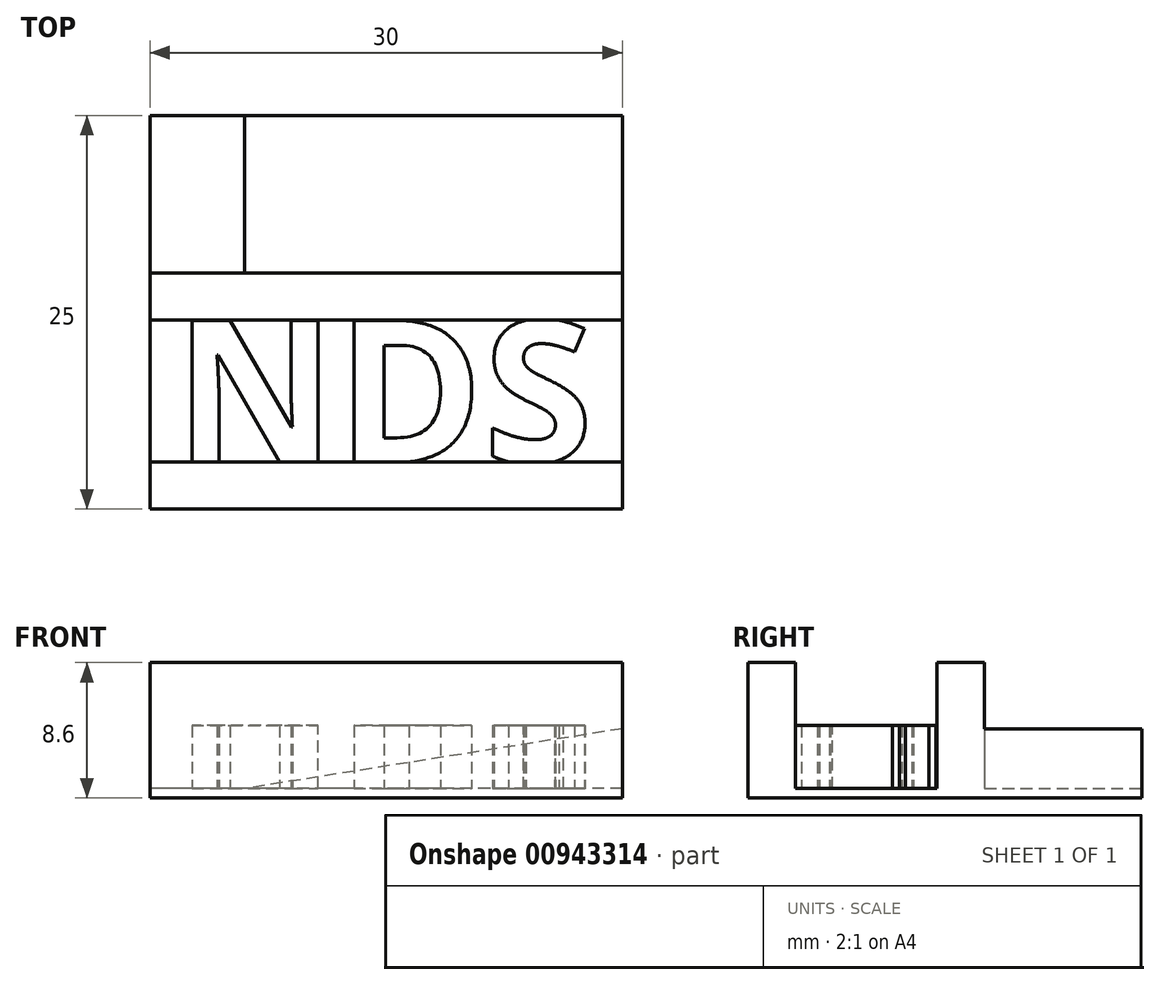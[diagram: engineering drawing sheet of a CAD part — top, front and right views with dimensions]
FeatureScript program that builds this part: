
annotation { "Feature Type Name" : "Feature", "Feature Type Description" : "" }
export const myFeature = defineFeature(function(context is Context, id is Id, definition is map)
    precondition{}
    {
        {
            var Q0;
            Q0=qCreatedBy(makeId("Top.planeOp"),FACE);
            var sketch = newSketch(context, id + "F0", { "sketchPlane" : qUnion([Q0])});
            skLineSegment(sketch, "E0.bottom", {"start": v(0, 0) * mm, "end": v(-30, 0) * mm});
            skLineSegment(sketch, "E0.top", {"start": v(0, 15) * mm, "end": v(-30, 15) * mm});
            skLineSegment(sketch, "E0.left", {"start": v(0, 0) * mm, "end": v(0, 15) * mm});
            skLineSegment(sketch, "E0.right", {"start": v(-30, 0) * mm, "end": v(-30, 15) * mm});
            skLineSegment(sketch, "E1.top", {"start": v(0, 25) * mm, "end": v(-30, 25) * mm});
            skLineSegment(sketch, "E1.left", {"start": v(0, 15) * mm, "end": v(0, 25) * mm});
            skLineSegment(sketch, "E1.right", {"start": v(-30, 15) * mm, "end": v(-30, 25) * mm});
            skSolve(sketch);
        }
        {
            var Q0;
            Q0=makeQuery(id+"F0.imprint","IMPRINT",FACE,{"disambiguationData":[TD([[makeQuery(id+"F0.imprint","IMPRINT",EDGE,{"derivedFrom":sQuery(id+"F0.wireOp",EDGE,"E0.top")}),-1.0]])]});
            var Q1;
            Q1=makeQuery(id+"F0.imprint","IMPRINT",FACE,{"disambiguationData":[TD([[makeQuery(id+"F0.imprint","IMPRINT",EDGE,{"derivedFrom":sQuery(id+"F0.wireOp",EDGE,"E0.bottom")}),-1.0]])]});
            extrude(context, id + "F1", {"entities" : qUnion([Q0, Q1]), "depth" : 0.6 * mm, "offsetDistance" : 25 * mm});
        }
        {
            var Q0;
            Q0=makeQuery(id+"F1.opExtrude","CAP_FACE",FACE,{"disambiguationData":[OSD([sQuery(id+"F0.wireOp",EDGE,"E0.bottom"),sQuery(id+"F0.wireOp",EDGE,"E0.left"),sQuery(id+"F0.wireOp",EDGE,"E0.right"),sQuery(id+"F0.wireOp",EDGE,"E1.top"),sQuery(id+"F0.wireOp",EDGE,"E1.left"),sQuery(id+"F0.wireOp",EDGE,"E1.right")])],"isStart":false});
            var sketch = newSketch(context, id + "F2", { "sketchPlane" : qUnion([Q0])});
            skLineSegment(sketch, "E2.bottom", {"start": v(0, 0) * mm, "end": v(-30, 0) * mm});
            skLineSegment(sketch, "E2.top", {"start": v(0, 15) * mm, "end": v(-30, 15) * mm});
            skLineSegment(sketch, "E2.left", {"start": v(0, 0) * mm, "end": v(0, 15) * mm});
            skLineSegment(sketch, "E2.right", {"start": v(-30, 0) * mm, "end": v(-30, 15) * mm});
            skLineSegment(sketch, "E3.top", {"start": v(0, 12) * mm, "end": v(-30, 12) * mm});
            skLineSegment(sketch, "E3.left", {"start": v(0, 15) * mm, "end": v(0, 12) * mm});
            skLineSegment(sketch, "E3.right", {"start": v(-30, 15) * mm, "end": v(-30, 12) * mm});
            skLineSegment(sketch, "E4.top", {"start": v(0, 3) * mm, "end": v(-30, 3) * mm});
            skLineSegment(sketch, "E4.left", {"start": v(0, 0) * mm, "end": v(0, 3) * mm});
            skLineSegment(sketch, "E4.right", {"start": v(-30, 0) * mm, "end": v(-30, 3) * mm});
            skSolve(sketch);
        }
        {
            var Q0;
            Q0=makeQuery(id+"F2.imprint","IMPRINT",FACE,{"disambiguationData":[TD([[makeQuery(id+"F2.imprint","IMPRINT",EDGE,{"derivedFrom":sQuery(id+"F2.wireOp",EDGE,"E2.top")}),1.0]])]});
            var Q1;
            Q1=makeQuery(id+"F2.imprint","IMPRINT",FACE,{"disambiguationData":[TD([[makeQuery(id+"F2.imprint","IMPRINT",EDGE,{"derivedFrom":sQuery(id+"F2.wireOp",EDGE,"E2.bottom")}),-1.0]])]});
            extrude(context, id + "F3", {"entities" : qUnion([Q0, Q1]), "operationType" : NewBodyOperationType.ADD, "depth" : 8 * mm, "offsetDistance" : 25 * mm});
        }
        {
            var Q0;
            Q0=makeQuery(id+"F3.opExtrude","SWEPT_FACE",FACE,{"disambiguationData":[OSD([sQuery(id+"F2.wireOp",EDGE,"E2.top")])]});
            var sketch = newSketch(context, id + "F4", { "sketchPlane" : qUnion([Q0])});
            skLineSegment(sketch, "E5.bottom", {"start": v(0, 8.6) * mm, "end": v(24, 8.6) * mm});
            skLineSegment(sketch, "E5.top", {"start": v(0, 0.6) * mm, "end": v(24, 0.6) * mm});
            skLineSegment(sketch, "E5.left", {"start": v(0, 8.6) * mm, "end": v(0, 0.6) * mm});
            skLineSegment(sketch, "E5.right", {"start": v(24, 8.6) * mm, "end": v(24, 0.6) * mm});
            skLineSegment(sketch, "E6", {"start": v(0, 0.6) * mm, "end": v(0, 4.4) * mm});
            skLineSegment(sketch, "E7", {"start": v(0, 4.4) * mm, "end": v(24, 0.6) * mm});
            skSolve(sketch);
        }
        {
            var Q0;
            Q0=makeQuery(id+"F4.imprint","IMPRINT",FACE,{"disambiguationData":[TD([[makeQuery(id+"F4.imprint","IMPRINT",EDGE,{"derivedFrom":sQuery(id+"F4.wireOp",EDGE,"E5.top")}),1.0]])]});
            extrude(context, id + "F5", {"entities" : qUnion([Q0]), "operationType" : NewBodyOperationType.ADD, "depth" : 10 * mm, "offsetDistance" : 25 * mm});
        }
        {
            var Q0;
            {var subQ0=sQuery(id+"F0.wireOp",EDGE,"E1.right");var subQ1=sQuery(id+"F0.wireOp",EDGE,"E0.right");var subQ2=sQuery(id+"F0.wireOp",EDGE,"E1.left");var subQ3=sQuery(id+"F0.wireOp",EDGE,"E0.left");Q0=makeQuery(id+"F3.boolean.opBoolean","SPLIT",FACE,{"disambiguationData":[TD([makeQuery(id+"F3.opExtrude","SWEPT_FACE",FACE,{"disambiguationData":[OSD([sQuery(id+"F2.wireOp",EDGE,"E3.top")])]})])],"derivedFrom":makeQuery(id+"F1.opExtrude","CAP_FACE",FACE,{"disambiguationData":[OSD([sQuery(id+"F0.wireOp",EDGE,"E0.bottom"),subQ3,subQ1,sQuery(id+"F0.wireOp",EDGE,"E1.top"),subQ2,subQ0])],"isStart":false})});}
            var sketch = newSketch(context, id + "F6", { "sketchPlane" : qUnion([Q0])});
            skText(sketch, "E8", { "text": "NDS", "fontName": "OpenSans-Bold.ttf"});
            skLineSegment(sketch, "E9", {"start": v(-28.46, 12.05) * mm, "end": v(-30, 12.05) * mm});
            skLineSegment(sketch, "E10", {"start": v(-1.54, 12.05) * mm, "end": v(0, 12.05) * mm});
            skLineSegment(sketch, "E11", {"start": v(-28.46, 12) * mm, "end": v(-28.46, 12.05) * mm});
            skLineSegment(sketch, "E12", {"start": v(-28.46, 3) * mm, "end": v(-28.46, 2.95) * mm});
            const initialGuessF6  = {"E8": [-0.02846, 0.00295, 1, 0, 0.0091]};
            skSetInitialGuess(sketch, initialGuessF6);
            skSolve(sketch);
        }
        {
            var Q0;
            Q0=makeQuery(id+"F6.imprint","IMPRINT",FACE,{"disambiguationData":[TD([[makeQuery(id+"F6.imprint","IMPRINT",EDGE,{"derivedFrom":sQuery(id+"F6.wireOp",EDGE,"E8.sketch_text.stroke-0")}),-1.0]])]});
            var Q1;
            Q1=makeQuery(id+"F6.imprint","IMPRINT",FACE,{"disambiguationData":[TD([[makeQuery(id+"F6.imprint","IMPRINT",EDGE,{"derivedFrom":sQuery(id+"F6.wireOp",EDGE,"E8.sketch_text.stroke-14")}),-1.0]])]});
            var Q2;
            Q2=makeQuery(id+"F6.imprint","IMPRINT",FACE,{"disambiguationData":[TD([[makeQuery(id+"F6.imprint","IMPRINT",EDGE,{"derivedFrom":sQuery(id+"F6.wireOp",EDGE,"E8.sketch_text.stroke-26")}),-1.0]])]});
            var Q3;
            {var subQ4=sQuery(id+"F6.wireOp",EDGE,"E8.sketch_text.stroke-2");Q3=makeQuery(id+"F6.imprint","IMPRINT",FACE,{"disambiguationData":[TD([[makeQuery(id+"F6.imprint","IMPRINT",EDGE,{"derivedFrom":subQ4}),-1.0]])]});}
            extrude(context, id + "F7", {"entities" : qUnion([Q0, Q1, Q2, Q3]), "operationType" : NewBodyOperationType.ADD, "depth" : 4 * mm, "offsetDistance" : 25 * mm});
        }
    });
